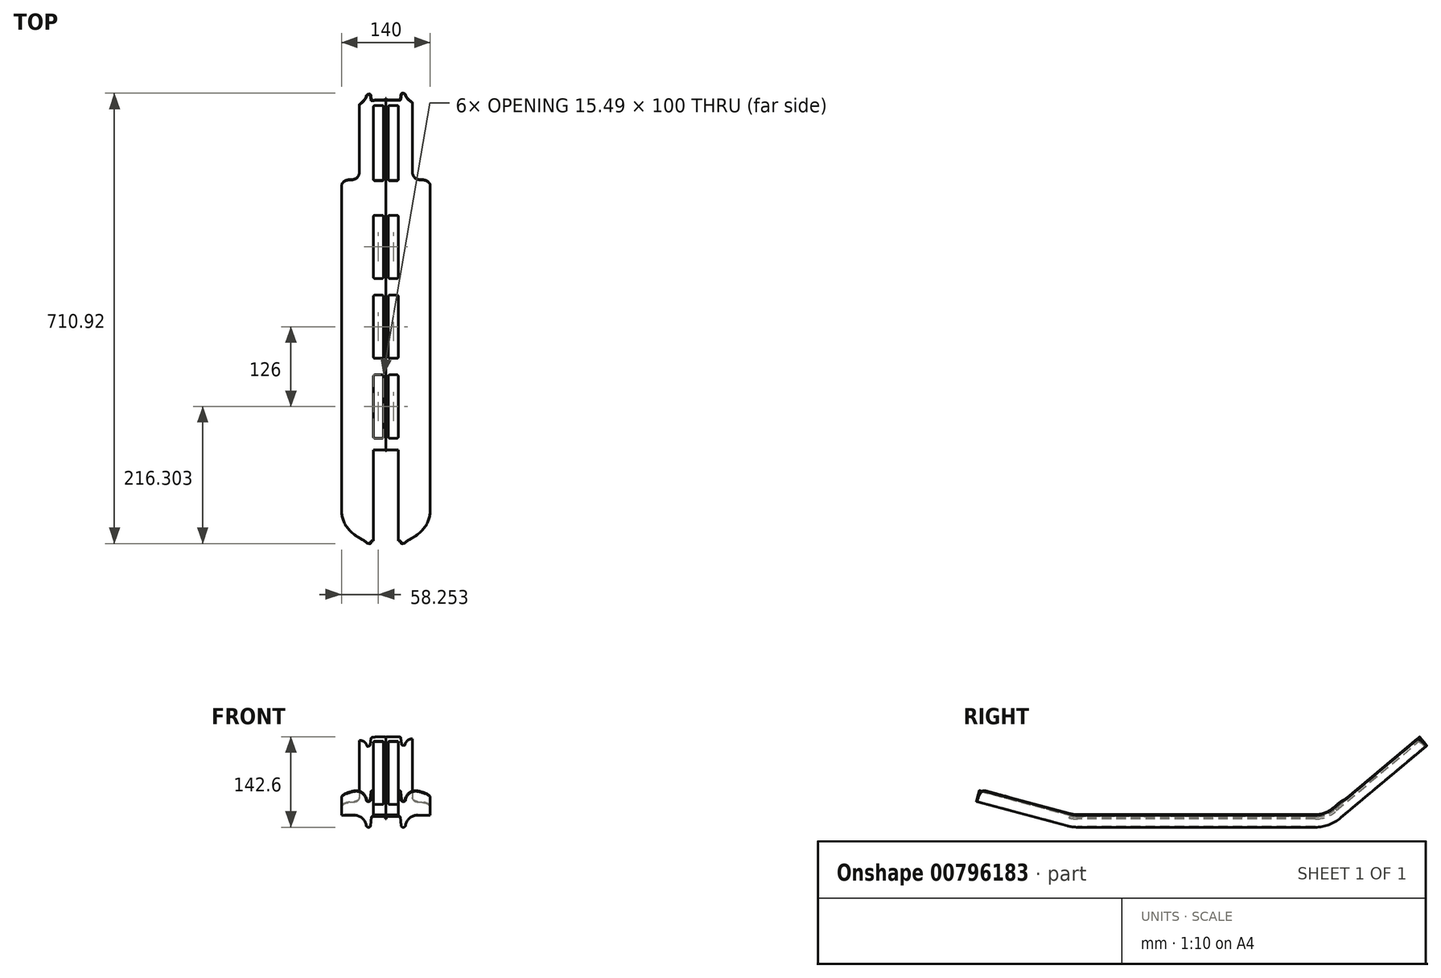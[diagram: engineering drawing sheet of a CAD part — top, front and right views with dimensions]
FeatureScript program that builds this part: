
annotation { "Feature Type Name" : "Feature", "Feature Type Description" : "" }
export const myFeature = defineFeature(function(context is Context, id is Id, definition is map)
    precondition{}
    {
        {
            var Q0;
            Q0=qCreatedBy(makeId("Front.planeOp"),FACE);
            var sketch = newSketch(context, id + "F0", { "sketchPlane" : qUnion([Q0])});
            skLineSegment(sketch, "E0", {"start": v(0, 0) * mm, "end": v(0, 3) * mm});
            skLineSegment(sketch, "E1", {"start": v(-2, 5) * mm, "end": v(-21.5, 5) * mm});
            skLineSegment(sketch, "E2", {"start": v(-23.48, 3.2) * mm, "end": v(-24.84, -10.2) * mm});
            skLineSegment(sketch, "E3", {"start": v(-26.83, -12) * mm, "end": v(-28.2, -12) * mm});
            skLineSegment(sketch, "E4", {"start": v(0, 0) * mm, "end": v(-70, 0) * mm, "construction": true});
            skLineSegment(sketch, "E5", {"start": v(0, 5) * mm, "end": v(0, 7) * mm, "construction": true});
            skLineSegment(sketch, "E6", {"start": v(-50, 7) * mm, "end": v(-70, 7) * mm});
            skArc(sketch, "E7", {"start": v(-50, 7) * mm, "mid": v(-36.86, 2.08) * mm, "end": v(-30.19, -10.27) * mm});
            skPoint(sketch, "E8.visualSharp", {"position": v(-23.3, 5) * mm});
            skArc(sketch, "E8.filletArc", {"start": v(-21.5, 5) * mm, "mid": v(-22.83, 4.48) * mm, "end": v(-23.48, 3.2) * mm});
            skPoint(sketch, "E9.visualSharp", {"position": v(0, 5) * mm});
            skArc(sketch, "E9.filletArc", {"start": v(0, 3) * mm, "mid": v(-0.59, 4.41) * mm, "end": v(-2, 5) * mm});
            skPoint(sketch, "E10.visualSharp", {"position": v(-25.03, -12) * mm});
            skArc(sketch, "E10.filletArc", {"start": v(-26.83, -12) * mm, "mid": v(-25.5, -11.48) * mm, "end": v(-24.84, -10.2) * mm});
            skPoint(sketch, "E11.visualSharp", {"position": v(-30.03, -12) * mm});
            skArc(sketch, "E11.filletArc", {"start": v(-30.19, -10.27) * mm, "mid": v(-29.52, -11.5) * mm, "end": v(-28.2, -12) * mm});
            skLineSegment(sketch, "E12.0", {"start": v(-50, 6.1) * mm, "end": v(-70, 6.1) * mm});
            skArc(sketch, "E12.1", {"start": v(-50, 6.1) * mm, "mid": v(-37.45, 1.4) * mm, "end": v(-31.08, -10.4) * mm});
            skArc(sketch, "E12.2", {"start": v(-31.08, -10.4) * mm, "mid": v(-30.11, -12.19) * mm, "end": v(-28.2, -12.9) * mm});
            skLineSegment(sketch, "E12.3", {"start": v(-26.83, -12.9) * mm, "end": v(-28.2, -12.9) * mm});
            skArc(sketch, "E12.4", {"start": v(-26.83, -12.9) * mm, "mid": v(-24.89, -12.15) * mm, "end": v(-23.95, -10.3) * mm});
            skLineSegment(sketch, "E12.5", {"start": v(-22.59, 3.11) * mm, "end": v(-23.95, -10.3) * mm});
            skLineSegment(sketch, "E12.6", {"start": v(-0.9, 0) * mm, "end": v(-0.9, 3) * mm});
            skArc(sketch, "E12.7", {"start": v(-0.9, 3) * mm, "mid": v(-1.22, 3.78) * mm, "end": v(-2, 4.1) * mm});
            skLineSegment(sketch, "E12.8", {"start": v(-2, 4.1) * mm, "end": v(-21.5, 4.1) * mm});
            skArc(sketch, "E12.9", {"start": v(-21.5, 4.1) * mm, "mid": v(-22.23, 3.82) * mm, "end": v(-22.59, 3.11) * mm});
            skLineSegment(sketch, "E13", {"start": v(-70, 7) * mm, "end": v(-70, 6.1) * mm});
            skLineSegment(sketch, "E14", {"start": v(-0.9, 0) * mm, "end": v(0, 0) * mm});
            skSolve(sketch);
        }
        {
            var Q0;
            Q0=qCreatedBy(makeId("Right.planeOp"),FACE);
            var sketch = newSketch(context, id + "F1", { "sketchPlane" : qUnion([Q0])});
            skLineSegment(sketch, "E15", {"start": v(0, 0) * mm, "end": v(-193.42, 0) * mm});
            skLineSegment(sketch, "E16", {"start": v(-206.36, 1.7) * mm, "end": v(-350, 40.2) * mm});
            skLineSegment(sketch, "E17", {"start": v(0, 0) * mm, "end": v(181.8, 0) * mm});
            skLineSegment(sketch, "E18", {"start": v(213.94, 11.7) * mm, "end": v(350, 125.86) * mm});
            skPoint(sketch, "E19.visualSharp", {"position": v(-200, 0) * mm});
            skArc(sketch, "E19.filletArc", {"start": v(-206.36, 1.7) * mm, "mid": v(-199.94, 0.43) * mm, "end": v(-193.42, 0) * mm});
            skPoint(sketch, "E20.visualSharp", {"position": v(200, 0) * mm});
            skArc(sketch, "E20.filletArc", {"start": v(181.8, 0) * mm, "mid": v(198.9, 3.02) * mm, "end": v(213.94, 11.7) * mm});
            skSolve(sketch);
        }
        {
            var Q0;
            Q0=makeQuery(id+"F0.imprint","IMPRINT",FACE,{"disambiguationData":[TD([[makeQuery(id+"F0.imprint","IMPRINT",EDGE,{"derivedFrom":sQuery(id+"F0.wireOp",EDGE,"E0")}),1.0]])]});
            var Q1;
            Q1=sQuery(id+"F1.wireOp",EDGE,"E15");
            var Q2;
            Q2=sQuery(id+"F1.wireOp",EDGE,"E17");
            var Q3;
            Q3=sQuery(id+"F1.wireOp",EDGE,"E19.filletArc");
            var Q4;
            Q4=sQuery(id+"F1.wireOp",EDGE,"E16");
            var Q5;
            Q5=sQuery(id+"F1.wireOp",EDGE,"E20.filletArc");
            var Q6;
            Q6=sQuery(id+"F1.wireOp",EDGE,"E18");
            sweep(context, id + "F2", {"profiles" : qUnion([Q0]), "path" : qUnion([Q1, Q2, Q3, Q4, Q5, Q6])});
        }
        {
            var Q0;
            Q0=makeQuery(id+"F2.opSweep","SWEPT_BODY",BODY,{"disambiguationData":[OSD([sQuery(id+"F0.wireOp",EDGE,"E0"),sQuery(id+"F0.wireOp",EDGE,"E1"),sQuery(id+"F0.wireOp",EDGE,"E2"),sQuery(id+"F0.wireOp",EDGE,"E3"),sQuery(id+"F0.wireOp",EDGE,"E6"),sQuery(id+"F0.wireOp",EDGE,"E7"),sQuery(id+"F0.wireOp",EDGE,"E8.filletArc"),sQuery(id+"F0.wireOp",EDGE,"E9.filletArc"),sQuery(id+"F0.wireOp",EDGE,"E10.filletArc"),sQuery(id+"F0.wireOp",EDGE,"E11.filletArc"),sQuery(id+"F0.wireOp",EDGE,"E12.0"),sQuery(id+"F0.wireOp",EDGE,"E12.1"),sQuery(id+"F0.wireOp",EDGE,"E12.2"),sQuery(id+"F0.wireOp",EDGE,"E12.3"),sQuery(id+"F0.wireOp",EDGE,"E12.4"),sQuery(id+"F0.wireOp",EDGE,"E12.5"),sQuery(id+"F0.wireOp",EDGE,"E12.6"),sQuery(id+"F0.wireOp",EDGE,"E12.7"),sQuery(id+"F0.wireOp",EDGE,"E12.8"),sQuery(id+"F0.wireOp",EDGE,"E12.9"),sQuery(id+"F0.wireOp",EDGE,"E13"),sQuery(id+"F0.wireOp",EDGE,"E14"),sQuery(id+"F1.wireOp",EDGE,"E18")])]});
            var Q1;
            Q1=qCreatedBy(makeId("Right.planeOp"),FACE);
            mirror(context, id + "F3", {"operationType" : NewBodyOperationType.ADD, "entities" : qUnion([Q0]), "mirrorPlane" : qUnion([Q1])});
        }
        {
            var Q0;
            Q0=makeQuery(id+"F2.opSweep","SWEPT_FACE",FACE,{"disambiguationData":[OSD([sQuery(id+"F0.wireOp",EDGE,"E1"),sQuery(id+"F1.wireOp",EDGE,"E16")])]});
            var sketch = newSketch(context, id + "F4", { "sketchPlane" : qUnion([Q0])});
            skLineSegment(sketch, "E21.bottom", {"start": v(-19.5, -199.77) * mm, "end": v(19.5, -199.77) * mm});
            skLineSegment(sketch, "E21.top", {"start": v(-19.5, -359.77) * mm, "end": v(19.5, -359.77) * mm});
            skLineSegment(sketch, "E21.left", {"start": v(-19.5, -199.77) * mm, "end": v(-19.5, -359.77) * mm});
            skLineSegment(sketch, "E21.right", {"start": v(19.5, -199.77) * mm, "end": v(19.5, -359.77) * mm});
            skSolve(sketch);
        }
        {
            var Q0;
            {var subQ2=sQuery(id+"F4.wireOp",EDGE,"E21.top");Q0=makeQuery(id+"F4.imprint","IMPRINT",FACE,{"disambiguationData":[TD([[makeQuery(id+"F4.imprint","IMPRINT",EDGE,{"derivedFrom":subQ2}),1.0]])]});}
            var Q1;
            {var subQ1=sQuery(id+"F0.wireOp",EDGE,"E1");var subQ2=makeQuery(id+"F2.opSweep","SWEPT_EDGE",EDGE,{"disambiguationData":[OSD([subQ1,sQuery(id+"F0.wireOp",EDGE,"E9.filletArc"),sQuery(id+"F1.wireOp",EDGE,"E16")])]});Q1=makeQuery(id+"F4.imprint","IMPRINT",FACE,{"disambiguationData":[TD([[makeQuery(id+"F4.imprint","IMPRINT",EDGE,{"derivedFrom":subQ2}),-1.0]])]});}
            extrude(context, id + "F5", {"entities" : qUnion([Q0, Q1]), "operationType" : NewBodyOperationType.REMOVE, "oppositeDirection" : true, "depth" : 25 * mm, "offsetDistance" : 25 * mm});
        }
        {
            var Q0;
            Q0=makeQuery(id+"F2.opSweep","CAP_EDGE",EDGE,{"disambiguationData":[OSD([sQuery(id+"F0.wireOp",EDGE,"E13"),sQuery(id+"F1.wireOp",VERTEX,"E18.end")])],"isStart":true});
            fillet(context, id + "F6", {"entities" : qUnion([Q0]), "radius" : 60.1 * mm, "tangentPropagation" : true, "allowEdgeOverflow" : false});
        }
        {
            var Q0;
            Q0=makeQuery(id+"F3.opPattern","COPY",EDGE,{"derivedFrom":makeQuery(id+"F2.opSweep","CAP_EDGE",EDGE,{"disambiguationData":[OSD([sQuery(id+"F0.wireOp",EDGE,"E13"),sQuery(id+"F1.wireOp",VERTEX,"E18.end")])],"isStart":true}),"instanceName":"1"});
            fillet(context, id + "F7", {"entities" : qUnion([Q0]), "radius" : 50 * mm, "tangentPropagation" : true, "allowEdgeOverflow" : false});
        }
        {
            var Q0;
            Q0=makeQuery(id+"F2.opSweep","SWEPT_FACE",FACE,{"disambiguationData":[OSD([sQuery(id+"F0.wireOp",EDGE,"E1"),sQuery(id+"F1.wireOp",EDGE,"E17")])]});
            var sketch = newSketch(context, id + "F8", { "sketchPlane" : qUnion([Q0])});
            skLineSegment(sketch, "E22.bottom", {"start": v(-17.5, -186.66) * mm, "end": v(-6, -186.66) * mm});
            skLineSegment(sketch, "E22.top", {"start": v(-17.5, -86.66) * mm, "end": v(-6, -86.66) * mm});
            skLineSegment(sketch, "E22.left", {"start": v(-19.5, -184.66) * mm, "end": v(-19.5, -88.66) * mm});
            skLineSegment(sketch, "E22.right", {"start": v(-4, -184.66) * mm, "end": v(-4, -88.66) * mm});
            skPoint(sketch, "E23.visualSharp", {"position": v(-19.5, -186.66) * mm});
            skArc(sketch, "E23.filletArc", {"start": v(-19.5, -184.66) * mm, "mid": v(-18.9, -186.07) * mm, "end": v(-17.5, -186.66) * mm});
            skPoint(sketch, "E24.visualSharp", {"position": v(-4, -186.66) * mm});
            skArc(sketch, "E24.filletArc", {"start": v(-6, -186.66) * mm, "mid": v(-4.59, -186.07) * mm, "end": v(-4, -184.66) * mm});
            skPoint(sketch, "E25.visualSharp", {"position": v(-19.5, -86.66) * mm});
            skArc(sketch, "E25.filletArc", {"start": v(-17.5, -86.66) * mm, "mid": v(-18.9, -87.24) * mm, "end": v(-19.5, -88.66) * mm});
            skPoint(sketch, "E26.visualSharp", {"position": v(-4, -86.66) * mm});
            skArc(sketch, "E26.filletArc", {"start": v(-4, -88.66) * mm, "mid": v(-4.59, -87.24) * mm, "end": v(-6, -86.66) * mm});
            skLineSegment(sketch, "E27.0.1.0", {"start": v(-17.5, 39.34) * mm, "end": v(-6, 39.34) * mm});
            skArc(sketch, "E27.0.1.1", {"start": v(-17.5, 39.34) * mm, "mid": v(-18.9, 38.76) * mm, "end": v(-19.5, 37.34) * mm});
            skLineSegment(sketch, "E27.0.1.2", {"start": v(-19.5, -58.66) * mm, "end": v(-19.5, 37.34) * mm});
            skArc(sketch, "E27.0.1.3", {"start": v(-4, 37.34) * mm, "mid": v(-4.59, 38.76) * mm, "end": v(-6, 39.34) * mm});
            skLineSegment(sketch, "E27.0.1.4", {"start": v(-4, -58.66) * mm, "end": v(-4, 37.34) * mm});
            skArc(sketch, "E27.0.1.5", {"start": v(-6, -60.66) * mm, "mid": v(-4.59, -60.07) * mm, "end": v(-4, -58.66) * mm});
            skLineSegment(sketch, "E27.0.1.6", {"start": v(-17.5, -60.66) * mm, "end": v(-6, -60.66) * mm});
            skArc(sketch, "E27.0.1.7", {"start": v(-19.5, -58.66) * mm, "mid": v(-18.9, -60.07) * mm, "end": v(-17.5, -60.66) * mm});
            skLineSegment(sketch, "E27.0.2.0", {"start": v(-17.5, 165.34) * mm, "end": v(-6, 165.34) * mm});
            skArc(sketch, "E27.0.2.1", {"start": v(-17.5, 165.34) * mm, "mid": v(-18.9, 164.76) * mm, "end": v(-19.5, 163.34) * mm});
            skLineSegment(sketch, "E27.0.2.2", {"start": v(-19.5, 67.34) * mm, "end": v(-19.5, 163.34) * mm});
            skArc(sketch, "E27.0.2.3", {"start": v(-4, 163.34) * mm, "mid": v(-4.59, 164.76) * mm, "end": v(-6, 165.34) * mm});
            skLineSegment(sketch, "E27.0.2.4", {"start": v(-4, 67.34) * mm, "end": v(-4, 163.34) * mm});
            skArc(sketch, "E27.0.2.5", {"start": v(-6, 65.34) * mm, "mid": v(-4.59, 65.93) * mm, "end": v(-4, 67.34) * mm});
            skLineSegment(sketch, "E27.0.2.6", {"start": v(-17.5, 65.34) * mm, "end": v(-6, 65.34) * mm});
            skArc(sketch, "E27.0.2.7", {"start": v(-19.5, 67.34) * mm, "mid": v(-18.9, 65.93) * mm, "end": v(-17.5, 65.34) * mm});
            skLineSegment(sketch, "E27.1.0.0", {"start": v(6, -86.66) * mm, "end": v(17.5, -86.66) * mm});
            skArc(sketch, "E27.1.0.1", {"start": v(6, -86.66) * mm, "mid": v(4.6, -87.24) * mm, "end": v(4, -88.66) * mm});
            skLineSegment(sketch, "E27.1.0.2", {"start": v(4, -184.66) * mm, "end": v(4, -88.66) * mm});
            skArc(sketch, "E27.1.0.3", {"start": v(19.5, -88.66) * mm, "mid": v(18.91, -87.24) * mm, "end": v(17.5, -86.66) * mm});
            skLineSegment(sketch, "E27.1.0.4", {"start": v(19.5, -184.66) * mm, "end": v(19.5, -88.66) * mm});
            skArc(sketch, "E27.1.0.5", {"start": v(17.5, -186.66) * mm, "mid": v(18.91, -186.07) * mm, "end": v(19.5, -184.66) * mm});
            skLineSegment(sketch, "E27.1.0.6", {"start": v(6, -186.66) * mm, "end": v(17.5, -186.66) * mm});
            skArc(sketch, "E27.1.0.7", {"start": v(4, -184.66) * mm, "mid": v(4.6, -186.07) * mm, "end": v(6, -186.66) * mm});
            skLineSegment(sketch, "E27.1.1.0", {"start": v(6, 39.34) * mm, "end": v(17.5, 39.34) * mm});
            skArc(sketch, "E27.1.1.1", {"start": v(6, 39.34) * mm, "mid": v(4.6, 38.76) * mm, "end": v(4, 37.34) * mm});
            skLineSegment(sketch, "E27.1.1.2", {"start": v(4, -58.66) * mm, "end": v(4, 37.34) * mm});
            skArc(sketch, "E27.1.1.3", {"start": v(19.5, 37.34) * mm, "mid": v(18.91, 38.76) * mm, "end": v(17.5, 39.34) * mm});
            skLineSegment(sketch, "E27.1.1.4", {"start": v(19.5, -58.66) * mm, "end": v(19.5, 37.34) * mm});
            skArc(sketch, "E27.1.1.5", {"start": v(17.5, -60.66) * mm, "mid": v(18.91, -60.07) * mm, "end": v(19.5, -58.66) * mm});
            skLineSegment(sketch, "E27.1.1.6", {"start": v(6, -60.66) * mm, "end": v(17.5, -60.66) * mm});
            skArc(sketch, "E27.1.1.7", {"start": v(4, -58.66) * mm, "mid": v(4.6, -60.07) * mm, "end": v(6, -60.66) * mm});
            skLineSegment(sketch, "E27.1.2.0", {"start": v(6, 165.34) * mm, "end": v(17.5, 165.34) * mm});
            skArc(sketch, "E27.1.2.1", {"start": v(6, 165.34) * mm, "mid": v(4.6, 164.76) * mm, "end": v(4, 163.34) * mm});
            skLineSegment(sketch, "E27.1.2.2", {"start": v(4, 67.34) * mm, "end": v(4, 163.34) * mm});
            skArc(sketch, "E27.1.2.3", {"start": v(19.5, 163.34) * mm, "mid": v(18.91, 164.76) * mm, "end": v(17.5, 165.34) * mm});
            skLineSegment(sketch, "E27.1.2.4", {"start": v(19.5, 67.34) * mm, "end": v(19.5, 163.34) * mm});
            skArc(sketch, "E27.1.2.5", {"start": v(17.5, 65.34) * mm, "mid": v(18.91, 65.93) * mm, "end": v(19.5, 67.34) * mm});
            skLineSegment(sketch, "E27.1.2.6", {"start": v(6, 65.34) * mm, "end": v(17.5, 65.34) * mm});
            skArc(sketch, "E27.1.2.7", {"start": v(4, 67.34) * mm, "mid": v(4.6, 65.93) * mm, "end": v(6, 65.34) * mm});
            skLineSegment(sketch, "E27.direction1", {"start": v(-17.5, -86.66) * mm, "end": v(6, -86.66) * mm, "construction": true});
            skLineSegment(sketch, "E27.direction2", {"start": v(-17.5, -86.66) * mm, "end": v(-17.5, 39.34) * mm, "construction": true});
            skSolve(sketch);
        }
        {
            var Q0;
            Q0 = qSketchRegion(id + "F8", true);
            extrude(context, id + "F9", {"entities" : qUnion([Q0]), "operationType" : NewBodyOperationType.REMOVE, "oppositeDirection" : true, "depth" : 25 * mm, "offsetDistance" : 25 * mm});
        }
        {
            var Q0;
            Q0=makeQuery(id+"F3.opPattern","COPY",FACE,{"derivedFrom":makeQuery(id+"F2.opSweep","SWEPT_FACE",FACE,{"disambiguationData":[OSD([sQuery(id+"F0.wireOp",EDGE,"E1"),sQuery(id+"F1.wireOp",EDGE,"E18")])]}),"instanceName":"1"});
            var sketch = newSketch(context, id + "F10", { "sketchPlane" : qUnion([Q0])});
            skLineSegment(sketch, "E28.bottom", {"start": v(17.5, 338.17) * mm, "end": v(6, 338.17) * mm});
            skLineSegment(sketch, "E28.top", {"start": v(17.5, 183.17) * mm, "end": v(6, 183.17) * mm});
            skLineSegment(sketch, "E28.left", {"start": v(19.5, 336.17) * mm, "end": v(19.5, 185.17) * mm});
            skLineSegment(sketch, "E28.right", {"start": v(4, 336.17) * mm, "end": v(4, 185.17) * mm});
            skPoint(sketch, "E29.visualSharp", {"position": v(19.5, 338.17) * mm});
            skArc(sketch, "E29.filletArc", {"start": v(19.5, 336.17) * mm, "mid": v(18.9, 337.58) * mm, "end": v(17.5, 338.17) * mm});
            skPoint(sketch, "E30.visualSharp", {"position": v(4, 338.17) * mm});
            skArc(sketch, "E30.filletArc", {"start": v(6, 338.17) * mm, "mid": v(4.59, 337.58) * mm, "end": v(4, 336.17) * mm});
            skPoint(sketch, "E31.visualSharp", {"position": v(4, 183.17) * mm});
            skArc(sketch, "E31.filletArc", {"start": v(4, 185.17) * mm, "mid": v(4.59, 183.75) * mm, "end": v(6, 183.17) * mm});
            skPoint(sketch, "E32.visualSharp", {"position": v(19.5, 183.17) * mm});
            skArc(sketch, "E32.filletArc", {"start": v(17.5, 183.17) * mm, "mid": v(18.9, 183.75) * mm, "end": v(19.5, 185.17) * mm});
            skArc(sketch, "E33.1.0.0", {"start": v(-3.9, 336.17) * mm, "mid": v(-4.5, 337.58) * mm, "end": v(-5.9, 338.17) * mm});
            skLineSegment(sketch, "E33.1.0.1", {"start": v(-3.9, 336.17) * mm, "end": v(-3.9, 185.17) * mm});
            skLineSegment(sketch, "E33.1.0.2", {"start": v(-5.9, 338.17) * mm, "end": v(-17.4, 338.17) * mm});
            skArc(sketch, "E33.1.0.3", {"start": v(-17.4, 338.17) * mm, "mid": v(-18.81, 337.58) * mm, "end": v(-19.4, 336.17) * mm});
            skLineSegment(sketch, "E33.1.0.4", {"start": v(-19.4, 336.17) * mm, "end": v(-19.4, 185.17) * mm});
            skPoint(sketch, "E33.1.0.5", {"position": v(-3.9, 183.17) * mm});
            skArc(sketch, "E33.1.0.6", {"start": v(-5.9, 183.17) * mm, "mid": v(-4.5, 183.75) * mm, "end": v(-3.9, 185.17) * mm});
            skLineSegment(sketch, "E33.1.0.7", {"start": v(-5.9, 183.17) * mm, "end": v(-17.4, 183.17) * mm});
            skArc(sketch, "E33.1.0.8", {"start": v(-19.4, 185.17) * mm, "mid": v(-18.81, 183.75) * mm, "end": v(-17.4, 183.17) * mm});
            skLineSegment(sketch, "E33.direction1", {"start": v(17.5, 336.17) * mm, "end": v(-5.9, 336.17) * mm, "construction": true});
            skLineSegment(sketch, "E34.bottom", {"start": v(-93.25, 346.8) * mm, "end": v(-42.03, 346.8) * mm});
            skLineSegment(sketch, "E34.top", {"start": v(-93.25, 186.4) * mm, "end": v(-42.03, 186.4) * mm});
            skLineSegment(sketch, "E34.left", {"start": v(-93.25, 346.8) * mm, "end": v(-93.25, 186.4) * mm});
            skLineSegment(sketch, "E34.right", {"start": v(-42.03, 346.8) * mm, "end": v(-42.03, 186.4) * mm});
            skLineSegment(sketch, "E35.MirrorCS", {"start": v(93.25, 346.8) * mm, "end": v(93.25, 186.4) * mm});
            skLineSegment(sketch, "E36.MirrorCS", {"start": v(93.25, 346.8) * mm, "end": v(42.03, 346.8) * mm});
            skLineSegment(sketch, "E37.MirrorCS", {"start": v(42.03, 346.8) * mm, "end": v(42.03, 186.4) * mm});
            skLineSegment(sketch, "E38.MirrorCS", {"start": v(93.25, 186.4) * mm, "end": v(42.03, 186.4) * mm});
            skSolve(sketch);
        }
        {
            var Q0;
            Q0 = qSketchRegion(id + "F10", true);
            extrude(context, id + "F11", {"entities" : qUnion([Q0]), "operationType" : NewBodyOperationType.REMOVE, "oppositeDirection" : true, "depth" : 25 * mm, "offsetDistance" : 25 * mm});
        }
        {
            var Q0;
            Q0=makeQuery(id+"F3.opPattern","COPY",EDGE,{"derivedFrom":makeQuery(id+"F2.opSweep","CAP_EDGE",EDGE,{"disambiguationData":[OSD([sQuery(id+"F0.wireOp",EDGE,"E13"),sQuery(id+"F1.wireOp",VERTEX,"E16.end")])],"isStart":false}),"instanceName":"1"});
            var Q1;
            Q1=makeQuery(id+"F2.opSweep","CAP_EDGE",EDGE,{"disambiguationData":[OSD([sQuery(id+"F0.wireOp",EDGE,"E13"),sQuery(id+"F1.wireOp",VERTEX,"E16.end")])],"isStart":false});
            fillet(context, id + "F12", {"entities" : qUnion([Q0, Q1]), "radius" : 50 * mm, "tangentPropagation" : true, "allowEdgeOverflow" : false});
        }
        {
            var Q0;
            Q0=makeQuery(id+"F2.opSweep","SWEPT_FACE",FACE,{"disambiguationData":[OSD([sQuery(id+"F0.wireOp",EDGE,"E6"),sQuery(id+"F1.wireOp",EDGE,"E18")])]});
            cPlane(context, id + "F13", {"entities" : qUnion([Q0]), "cplaneType" : CPlaneType.OFFSET, "offset" : 25 * mm, "width" : 150 * mm, "height" : 150 * mm});
        }
        {
            var Q0;
            Q0=qCreatedBy(id+"F13.planeOp",FACE);
            var sketch = newSketch(context, id + "F14", { "sketchPlane" : qUnion([Q0])});
            skLineSegment(sketch, "E39.0", {"start": v(-42.03, 346.8) * mm, "end": v(-42.03, 186.4) * mm});
            skLineSegment(sketch, "E40.0", {"start": v(42.03, 346.8) * mm, "end": v(42.03, 186.4) * mm});
            skLineSegment(sketch, "E41.0.0", {"start": v(42.03, 186.4) * mm, "end": v(93.25, 186.4) * mm});
            skLineSegment(sketch, "E41.0.1", {"start": v(93.25, 186.4) * mm, "end": v(93.25, 346.8) * mm});
            skLineSegment(sketch, "E41.0.2", {"start": v(93.25, 346.8) * mm, "end": v(42.03, 346.8) * mm});
            skLineSegment(sketch, "E42.0.0", {"start": v(-93.25, 346.8) * mm, "end": v(-93.25, 186.4) * mm});
            skLineSegment(sketch, "E42.0.1", {"start": v(-93.25, 186.4) * mm, "end": v(-42.03, 186.4) * mm});
            skLineSegment(sketch, "E42.0.2", {"start": v(-42.03, 186.4) * mm, "end": v(-42.03, 346.8) * mm});
            skLineSegment(sketch, "E42.0.3", {"start": v(-42.03, 346.8) * mm, "end": v(-93.25, 346.8) * mm});
            skSolve(sketch);
        }
        {
            var Q0;
            Q0 = qSketchRegion(id + "F14", true);
            extrude(context, id + "F15", {"entities" : qUnion([Q0]), "operationType" : NewBodyOperationType.REMOVE, "oppositeDirection" : true, "depth" : 30 * mm, "offsetDistance" : 25 * mm});
        }
        {
            var Q0;
            Q0=makeQuery(id+"F15.boolean.opBoolean","MERGE",EDGE,{"derivedFrom":[makeQuery(id+"F11.boolean.opBoolean","COPY",EDGE,{"derivedFrom":makeQuery(id+"F11.opExtrude","SWEPT_EDGE",EDGE,{"disambiguationData":[OSD([sQuery(id+"F10.wireOp",EDGE,"E37.MirrorCS"),sQuery(id+"F10.wireOp",EDGE,"E38.MirrorCS")])]})}),makeQuery(id+"F15.opExtrude","SWEPT_EDGE",EDGE,{"disambiguationData":[OSD([sQuery(id+"F14.wireOp",EDGE,"E41.0.0"),sQuery(id+"F14.wireOp",EDGE,"E40.0")])]})]});
            var Q1;
            Q1=makeQuery(id+"F15.boolean.opBoolean","MERGE",EDGE,{"derivedFrom":[makeQuery(id+"F11.boolean.opBoolean","COPY",EDGE,{"derivedFrom":makeQuery(id+"F11.opExtrude","SWEPT_EDGE",EDGE,{"disambiguationData":[OSD([sQuery(id+"F10.wireOp",EDGE,"E34.top"),sQuery(id+"F10.wireOp",EDGE,"E34.right")])]})}),makeQuery(id+"F15.opExtrude","SWEPT_EDGE",EDGE,{"disambiguationData":[OSD([sQuery(id+"F14.wireOp",EDGE,"E42.0.1"),sQuery(id+"F14.wireOp",EDGE,"E42.0.2")])]})]});
            var Q2;
            Q2=makeQuery(id+"F15.boolean.opBoolean","INTERSECT",EDGE,{"derivedFrom":[makeQuery(id+"F2.opSweep","SWEPT_FACE",FACE,{"disambiguationData":[OSD([sQuery(id+"F0.wireOp",EDGE,"E13"),sQuery(id+"F1.wireOp",EDGE,"E18")])]}),makeQuery(id+"F15.opExtrude","SWEPT_FACE",FACE,{"disambiguationData":[OSD([sQuery(id+"F14.wireOp",EDGE,"E42.0.1")])]})]});
            var Q3;
            Q3=makeQuery(id+"F15.boolean.opBoolean","INTERSECT",EDGE,{"derivedFrom":[makeQuery(id+"F3.opPattern","COPY",FACE,{"derivedFrom":makeQuery(id+"F2.opSweep","SWEPT_FACE",FACE,{"disambiguationData":[OSD([sQuery(id+"F0.wireOp",EDGE,"E13"),sQuery(id+"F1.wireOp",EDGE,"E18")])]}),"instanceName":"1"}),makeQuery(id+"F15.opExtrude","SWEPT_FACE",FACE,{"disambiguationData":[OSD([sQuery(id+"F14.wireOp",EDGE,"E41.0.0")])]})]});
            fillet(context, id + "F16", {"entities" : qUnion([Q0, Q1, Q2, Q3]), "radius" : 13 * mm, "tangentPropagation" : true, "allowEdgeOverflow" : false});
        }
    });
